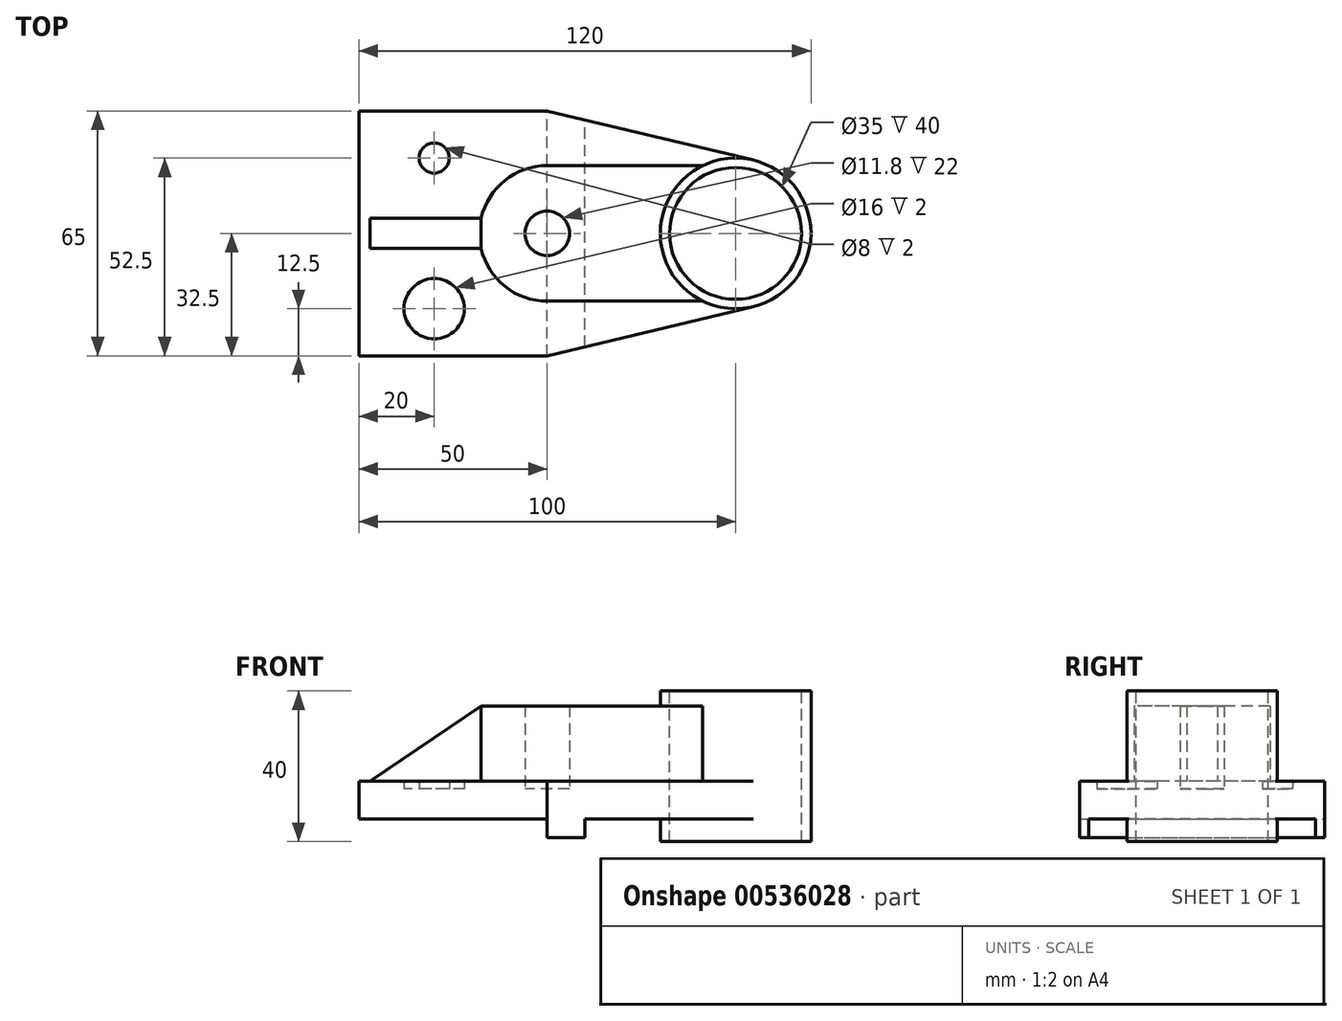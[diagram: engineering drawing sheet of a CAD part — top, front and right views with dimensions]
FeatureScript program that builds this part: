
annotation { "Feature Type Name" : "Feature", "Feature Type Description" : "" }
export const myFeature = defineFeature(function(context is Context, id is Id, definition is map)
    precondition{}
    {
        {
            var Q0;
            Q0=qCreatedBy(makeId("Top.planeOp"),FACE);
            var sketch = newSketch(context, id + "F0", { "sketchPlane" : qUnion([Q0])});
            skLineSegment(sketch, "E0.bottom", {"start": v(-50, 32.5) * mm, "end": v(50, 32.5) * mm});
            skLineSegment(sketch, "E0.top", {"start": v(-50, -32.5) * mm, "end": v(50, -32.5) * mm});
            skLineSegment(sketch, "E0.left", {"start": v(-50, 32.5) * mm, "end": v(-50, -32.5) * mm});
            skLineSegment(sketch, "E0.right", {"start": v(50, 32.5) * mm, "end": v(50, -32.5) * mm});
            skSolve(sketch);
        }
        {
            var Q0;
            Q0=makeQuery(id+"F0.imprint","IMPRINT",FACE,{"disambiguationData":[TD([[makeQuery(id+"F0.imprint","IMPRINT",EDGE,{"derivedFrom":sQuery(id+"F0.wireOp",EDGE,"E0.bottom")}),-1.0]])]});
            extrude(context, id + "F1", {"entities" : qUnion([Q0]), "depth" : 8 * mm, "offsetDistance" : 25 * mm});
        }
        {
            var Q0;
            Q0=makeQuery(id+"F1.opExtrude","CAP_FACE",FACE,{"disambiguationData":[OSD([sQuery(id+"F0.wireOp",EDGE,"E0.bottom"),sQuery(id+"F0.wireOp",EDGE,"E0.top"),sQuery(id+"F0.wireOp",EDGE,"E0.left"),sQuery(id+"F0.wireOp",EDGE,"E0.right")])],"isStart":true});
            var sketch = newSketch(context, id + "F2", { "sketchPlane" : qUnion([Q0])});
            skLineSegment(sketch, "E1.bottom", {"start": v(0, 32.5) * mm, "end": v(10, 32.5) * mm});
            skLineSegment(sketch, "E1.top", {"start": v(0, -32.5) * mm, "end": v(10, -32.5) * mm});
            skLineSegment(sketch, "E1.left", {"start": v(0, 32.5) * mm, "end": v(0, -32.5) * mm});
            skLineSegment(sketch, "E1.right", {"start": v(10, 32.5) * mm, "end": v(10, -32.5) * mm});
            skSolve(sketch);
        }
        {
            var Q0;
            Q0=makeQuery(id+"F2.imprint","IMPRINT",FACE,{"disambiguationData":[TD([[makeQuery(id+"F2.imprint","IMPRINT",EDGE,{"derivedFrom":sQuery(id+"F2.wireOp",EDGE,"E1.bottom")}),-1.0]])]});
            extrude(context, id + "F3", {"entities" : qUnion([Q0]), "operationType" : NewBodyOperationType.ADD, "depth" : 5 * mm, "offsetDistance" : 25 * mm});
        }
        {
            var Q0;
            Q0=makeQuery(id+"F1.opExtrude","CAP_FACE",FACE,{"disambiguationData":[OSD([sQuery(id+"F0.wireOp",EDGE,"E0.bottom"),sQuery(id+"F0.wireOp",EDGE,"E0.top"),sQuery(id+"F0.wireOp",EDGE,"E0.left"),sQuery(id+"F0.wireOp",EDGE,"E0.right")])],"isStart":false});
            var sketch = newSketch(context, id + "F4", { "sketchPlane" : qUnion([Q0])});
            skCircle(sketch, "E2", {"center": v(50, 0) * mm, "radius": 17.5 * mm});
            skCircle(sketch, "E3", {"center": v(50, 0) * mm, "radius": 20 * mm});
            skLineSegment(sketch, "E4", {"start": v(0, -32.5) * mm, "end": v(54.64, -19.45) * mm});
            skLineSegment(sketch, "E5", {"start": v(50, 0) * mm, "end": v(0, 0) * mm});
            skLineSegment(sketch, "E6.MirrorCS", {"start": v(0, 32.5) * mm, "end": v(54.64, 19.45) * mm});
            skSolve(sketch);
        }
        {
            var Q0;
            {var subQ0=sQuery(id+"F4.wireOp",EDGE,"E6.MirrorCS");var subQ1=makeQuery(id+"F1.opExtrude","CAP_EDGE",EDGE,{"disambiguationData":[OSD([sQuery(id+"F0.wireOp",EDGE,"E0.bottom")])],"isStart":false});var subQ2=makeQuery(id+"F4.imprint","INTERSECT",VERTEX,{"derivedFrom":[subQ1,subQ0]});Q0=makeQuery(id+"F4.imprint","IMPRINT",FACE,{"disambiguationData":[TD([[makeQuery(id+"F4.imprint","IMPRINT",EDGE,{"disambiguationData":[TD([[subQ2,-1.0]])],"derivedFrom":subQ0}),1.0]])]});}
            var Q1;
            {var subQ0=sQuery(id+"F4.wireOp",EDGE,"E4");var subQ1=makeQuery(id+"F1.opExtrude","CAP_EDGE",EDGE,{"disambiguationData":[OSD([sQuery(id+"F0.wireOp",EDGE,"E0.top")])],"isStart":false});var subQ2=makeQuery(id+"F4.imprint","INTERSECT",VERTEX,{"derivedFrom":[subQ1,subQ0]});Q1=makeQuery(id+"F4.imprint","IMPRINT",FACE,{"disambiguationData":[TD([[makeQuery(id+"F4.imprint","IMPRINT",EDGE,{"disambiguationData":[TD([[subQ2,-1.0]])],"derivedFrom":subQ0}),-1.0]])]});}
            extrude(context, id + "F5", {"entities" : qUnion([Q0, Q1]), "operationType" : NewBodyOperationType.REMOVE, "oppositeDirection" : true, "depth" : 25 * mm, "offsetDistance" : 25 * mm});
        }
        {
            var Q0;
            {var subQ0=sQuery(id+"F4.wireOp",EDGE,"E5");var subQ1=sQuery(id+"F4.wireOp",EDGE,"E2");var subQ2=makeQuery(id+"F4.imprint","INTERSECT",VERTEX,{"derivedFrom":[subQ1,subQ0]});Q0=makeQuery(id+"F4.imprint","IMPRINT",FACE,{"disambiguationData":[TD([[makeQuery(id+"F4.imprint","IMPRINT",EDGE,{"disambiguationData":[TD([[subQ2,-1.0]])],"derivedFrom":subQ1}),1.0]])]});}
            var Q1;
            {var subQ0=sQuery(id+"F4.wireOp",EDGE,"E5");var subQ1=sQuery(id+"F4.wireOp",EDGE,"E2");var subQ2=makeQuery(id+"F4.imprint","INTERSECT",VERTEX,{"derivedFrom":[subQ1,subQ0]});Q1=makeQuery(id+"F4.imprint","IMPRINT",FACE,{"disambiguationData":[TD([[makeQuery(id+"F4.imprint","IMPRINT",EDGE,{"disambiguationData":[TD([[subQ2,1.0]])],"derivedFrom":subQ1}),1.0]])]});}
            extrude(context, id + "F6", {"entities" : qUnion([Q0, Q1]), "operationType" : NewBodyOperationType.REMOVE, "oppositeDirection" : true, "depth" : 25 * mm, "offsetDistance" : 25 * mm});
        }
        {
            var Q0;
            {var subQ0=sQuery(id+"F4.wireOp",EDGE,"E4");var subQ1=sQuery(id+"F4.wireOp",EDGE,"E3");var subQ2=makeQuery(id+"F4.imprint","INTERSECT",VERTEX,{"derivedFrom":[subQ1,subQ0]});Q0=makeQuery(id+"F4.imprint","IMPRINT",FACE,{"disambiguationData":[TD([[makeQuery(id+"F4.imprint","IMPRINT",EDGE,{"disambiguationData":[TD([[subQ2,1.0]])],"derivedFrom":subQ1}),-1.0]])]});}
            var Q1;
            {var subQ0=sQuery(id+"F4.wireOp",EDGE,"E6.MirrorCS");var subQ1=sQuery(id+"F4.wireOp",EDGE,"E3");var subQ2=makeQuery(id+"F4.imprint","INTERSECT",VERTEX,{"derivedFrom":[subQ1,subQ0]});Q1=makeQuery(id+"F4.imprint","IMPRINT",FACE,{"disambiguationData":[TD([[makeQuery(id+"F4.imprint","IMPRINT",EDGE,{"disambiguationData":[TD([[subQ2,-1.0]])],"derivedFrom":subQ1}),-1.0]])]});}
            extrude(context, id + "F7", {"entities" : qUnion([Q0, Q1]), "operationType" : NewBodyOperationType.ADD, "oppositeDirection" : true, "depth" : 8 * mm, "offsetDistance" : 25 * mm});
        }
        {
            var Q0;
            {var subQ0=sQuery(id+"F4.wireOp",EDGE,"E5");var subQ1=sQuery(id+"F4.wireOp",EDGE,"E2");var subQ2=makeQuery(id+"F4.imprint","INTERSECT",VERTEX,{"derivedFrom":[subQ1,subQ0]});Q0=makeQuery(id+"F4.imprint","IMPRINT",FACE,{"disambiguationData":[TD([[makeQuery(id+"F4.imprint","IMPRINT",EDGE,{"disambiguationData":[TD([[subQ2,1.0]])],"derivedFrom":subQ1}),-1.0]])]});}
            var Q1;
            {var subQ2=makeQuery(id+"F1.opExtrude","CAP_EDGE",EDGE,{"disambiguationData":[OSD([sQuery(id+"F0.wireOp",EDGE,"E0.right")])],"isStart":false});var subQ6=sQuery(id+"F4.wireOp",EDGE,"E2");var subQ7=makeQuery(id+"F4.imprint","INTERSECT",VERTEX,{"disambiguationData":[OD(0.0)],"derivedFrom":[subQ2,subQ6]});Q1=makeQuery(id+"F4.imprint","IMPRINT",FACE,{"disambiguationData":[TD([[makeQuery(id+"F4.imprint","IMPRINT",EDGE,{"disambiguationData":[TD([[subQ7,1.0]])],"derivedFrom":subQ6}),-1.0]])]});}
            var Q2;
            {var subQ0=sQuery(id+"F4.wireOp",EDGE,"E5");var subQ1=sQuery(id+"F4.wireOp",EDGE,"E2");var subQ2=makeQuery(id+"F4.imprint","INTERSECT",VERTEX,{"derivedFrom":[subQ1,subQ0]});Q2=makeQuery(id+"F4.imprint","IMPRINT",FACE,{"disambiguationData":[TD([[makeQuery(id+"F4.imprint","IMPRINT",EDGE,{"disambiguationData":[TD([[subQ2,-1.0]])],"derivedFrom":subQ1}),-1.0]])]});}
            extrude(context, id + "F8", {"entities" : qUnion([Q0, Q1, Q2]), "operationType" : NewBodyOperationType.ADD, "depth" : 26 * mm, "offsetDistance" : 25 * mm, "hasSecondDirection" : true, "secondDirectionOppositeDirection" : true, "secondDirectionDepth" : 14 * mm});
        }
        {
            var Q0;
            {var subQ13=makeQuery(id+"F1.opExtrude","CAP_EDGE",EDGE,{"disambiguationData":[OSD([sQuery(id+"F0.wireOp",EDGE,"E0.left")])],"isStart":false});Q0=makeQuery(id+"F4.imprint","IMPRINT",FACE,{"disambiguationData":[TD([[makeQuery(id+"F4.imprint","IMPRINT",EDGE,{"derivedFrom":subQ13}),1.0]])]});}
            var sketch = newSketch(context, id + "F9", { "sketchPlane" : qUnion([Q0])});
            skArc(sketch, "E7", {"start": v(0, 18) * mm, "mid": v(-18, 0) * mm, "end": v(0, -18) * mm});
            skLineSegment(sketch, "E8", {"start": v(0, 18) * mm, "end": v(41.28, 18) * mm});
            skLineSegment(sketch, "E9", {"start": v(0, -18) * mm, "end": v(41.28, -18) * mm});
            skArc(sketch, "E10", {"start": v(41.28, 18) * mm, "mid": v(30, 0) * mm, "end": v(41.28, -18) * mm});
            skCircle(sketch, "E11", {"center": v(0, 0) * mm, "radius": 5.9 * mm});
            skSolve(sketch);
        }
        {
            var Q0;
            Q0=makeQuery(id+"F9.imprint","IMPRINT",FACE,{"disambiguationData":[TD([[makeQuery(id+"F9.imprint","IMPRINT",EDGE,{"derivedFrom":sQuery(id+"F9.wireOp",EDGE,"E7")}),1.0]])]});
            extrude(context, id + "F10", {"entities" : qUnion([Q0]), "operationType" : NewBodyOperationType.ADD, "depth" : 22 * mm, "offsetDistance" : 25 * mm});
        }
        {
            var Q0;
            {var subQ0=sQuery(id+"F4.wireOp",EDGE,"E6.MirrorCS");var subQ1=sQuery(id+"F4.wireOp",EDGE,"E4");var subQ2=sQuery(id+"F0.wireOp",EDGE,"E0.top");var subQ3=sQuery(id+"F4.wireOp",EDGE,"E3");var subQ4=sQuery(id+"F0.wireOp",EDGE,"E0.left");var subQ5=sQuery(id+"F0.wireOp",EDGE,"E0.bottom");var subQ6=sQuery(id+"F0.wireOp",EDGE,"E0.right");Q0=makeQuery(id+"F10.boolean.opBoolean","SPLIT",FACE,{"disambiguationData":[TD([makeQuery(id+"F1.opExtrude","SWEPT_FACE",FACE,{"disambiguationData":[OSD([subQ5])]})])],"derivedFrom":makeQuery(id+"F7.boolean.opBoolean","MERGE",FACE,{"derivedFrom":[makeQuery(id+"F1.opExtrude","CAP_FACE",FACE,{"disambiguationData":[OSD([subQ5,subQ2,subQ4,subQ6])],"isStart":false}),makeQuery(id+"F7.opExtrude","CAP_FACE",FACE,{"disambiguationData":[OSD([subQ6,subQ3,subQ0])],"isStart":true}),makeQuery(id+"F7.opExtrude","CAP_FACE",FACE,{"disambiguationData":[OSD([subQ6,subQ3,subQ1])],"isStart":true})]})});}
            var sketch = newSketch(context, id + "F11", { "sketchPlane" : qUnion([Q0])});
            skLineSegment(sketch, "E12.bottom", {"start": v(-50, 4) * mm, "end": v(-14.89, 4) * mm});
            skLineSegment(sketch, "E12.top", {"start": v(-50, -4) * mm, "end": v(-14.89, -4) * mm});
            skLineSegment(sketch, "E12.left", {"start": v(-50, 4) * mm, "end": v(-50, -4) * mm});
            skLineSegment(sketch, "E12.right", {"start": v(-14.89, 4) * mm, "end": v(-14.89, -4) * mm});
            skSolve(sketch);
        }
        {
            var Q0;
            {var subQ0=sQuery(id+"F11.wireOp",EDGE,"E12.left");Q0=makeQuery(id+"F11.imprint","IMPRINT",FACE,{"disambiguationData":[TD([[makeQuery(id+"F11.imprint","IMPRINT",EDGE,{"derivedFrom":subQ0}),1.0]])]});}
            var Q1;
            Q1=sQuery(id+"F11.wireOp",EDGE,"E12.right");
            var Q2;
            Q2=sQuery(id+"F11.wireOp",EDGE,"E12.top");
            var Q3;
            Q3=sQuery(id+"F11.wireOp",EDGE,"E12.bottom");
            var Q4;
            Q4=sQuery(id+"F11.wireOp",EDGE,"E12.left");
            extrude(context, id + "F12", {"entities" : qUnion([Q0]), "surfaceEntities" : qUnion([Q1, Q2, Q3, Q4]), "depth" : 22 * mm, "offsetDistance" : 25 * mm});
        }
        {
            var Q0;
            Q0=makeQuery(id+"F12.opExtrude","SWEPT_FACE",FACE,{"disambiguationData":[OSD([sQuery(id+"F11.wireOp",EDGE,"E12.top")])]});
            var sketch = newSketch(context, id + "F13", { "sketchPlane" : qUnion([Q0])});
            skLineSegment(sketch, "E13", {"start": v(-50, 8) * mm, "end": v(-17.55, 30) * mm});
            skSolve(sketch);
        }
        {
            var Q0;
            Q0 = qSketchRegion(id + "F13", true);
            var Q1;
            Q1=makeQuery(id+"F13.imprint","IMPRINT",FACE,{"disambiguationData":[TD([[makeQuery(id+"F13.imprint","IMPRINT",EDGE,{"derivedFrom":sQuery(id+"F13.wireOp",EDGE,"E13")}),1.0]])]});
            extrude(context, id + "F14", {"entities" : qUnion([Q0, Q1]), "operationType" : NewBodyOperationType.REMOVE, "oppositeDirection" : true, "depth" : 25 * mm, "offsetDistance" : 25 * mm});
        }
        {
            var Q0;
            {var subQ0=sQuery(id+"F4.wireOp",EDGE,"E6.MirrorCS");var subQ1=sQuery(id+"F4.wireOp",EDGE,"E4");var subQ2=sQuery(id+"F0.wireOp",EDGE,"E0.top");var subQ3=sQuery(id+"F4.wireOp",EDGE,"E3");var subQ4=sQuery(id+"F0.wireOp",EDGE,"E0.left");var subQ5=sQuery(id+"F0.wireOp",EDGE,"E0.bottom");var subQ6=sQuery(id+"F0.wireOp",EDGE,"E0.right");Q0=makeQuery(id+"F10.boolean.opBoolean","SPLIT",FACE,{"disambiguationData":[TD([makeQuery(id+"F1.opExtrude","SWEPT_FACE",FACE,{"disambiguationData":[OSD([subQ5])]})])],"derivedFrom":makeQuery(id+"F7.boolean.opBoolean","MERGE",FACE,{"derivedFrom":[makeQuery(id+"F1.opExtrude","CAP_FACE",FACE,{"disambiguationData":[OSD([subQ5,subQ2,subQ4,subQ6])],"isStart":false}),makeQuery(id+"F7.opExtrude","CAP_FACE",FACE,{"disambiguationData":[OSD([subQ6,subQ3,subQ0])],"isStart":true}),makeQuery(id+"F7.opExtrude","CAP_FACE",FACE,{"disambiguationData":[OSD([subQ6,subQ3,subQ1])],"isStart":true})]})});}
            var sketch = newSketch(context, id + "F15", { "sketchPlane" : qUnion([Q0])});
            skLineSegment(sketch, "E14", {"start": v(-30, 0) * mm, "end": v(-50, 0) * mm});
            skCircle(sketch, "E15", {"center": v(-30, 20) * mm, "radius": 8 * mm});
            skCircle(sketch, "E16", {"center": v(-30, 20) * mm, "radius": 4 * mm});
            skCircle(sketch, "E17.MirrorC", {"center": v(-30, -20) * mm, "radius": 8 * mm});
            skCircle(sketch, "E18.MirrorC", {"center": v(-30, -20) * mm, "radius": 4 * mm});
            skSolve(sketch);
        }
        {
            var Q0;
            Q0=makeQuery(id+"F15.imprint","IMPRINT",FACE,{"disambiguationData":[TD([[makeQuery(id+"F15.imprint","IMPRINT",EDGE,{"derivedFrom":sQuery(id+"F15.wireOp",EDGE,"E15")}),1.0]])]});
            extrude(context, id + "F16", {"entities" : qUnion([Q0]), "operationType" : NewBodyOperationType.ADD, "depth" : 2 * mm, "offsetDistance" : 25 * mm});
        }
        {
            var Q0;
            Q0=makeQuery(id+"F15.imprint","IMPRINT",FACE,{"disambiguationData":[TD([[makeQuery(id+"F15.imprint","IMPRINT",EDGE,{"derivedFrom":sQuery(id+"F15.wireOp",EDGE,"E17.MirrorC")}),-1.0]])]});
            extrude(context, id + "F17", {"entities" : qUnion([Q0]), "operationType" : NewBodyOperationType.ADD, "depth" : 2 * mm, "offsetDistance" : 25 * mm});
        }
    });
